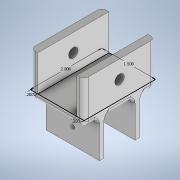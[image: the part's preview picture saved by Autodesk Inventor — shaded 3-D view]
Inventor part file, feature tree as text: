
AUTODESK INVENTOR PART (.ipt)
format: ipt  version: 2020 (Build 240168000, 168)  size: 201,728 bytes
history: native  units: in
note: dims shown in document units (in); Inventor stores cm internally (conversion verified against a paired STEP export)
features: sketch x4, extrude x3, hole x2, fillet x1
ambient origin geometry x8: Origin, YZ Plane, XZ Plane, XY Plane, X Axis, Y Axis, Z Axis, Center Point
bodies: Solid1 (feature_tree)
feature tree (10):
  sketch  "Sketch1"  dims[d0=1.5in d1=2.0in]
  extrude  "Extrusion1"  Depth=2.0in
  extrude  "Extrusion2"  Depth=0.2in
  hole  "Hole1"  [1 undecoded]
  extrude  "Extrusion3"  Depth=0.125in
  hole  "Hole2"  [1 undecoded]
  fillet  "Fillet1"  Radius=0.75in
  sketch  "Sketch2"  dims[d2=0.2in d3=0.2in]
  sketch  "Sketch3"  dims[d4=1.0in d5=0.0in d6=0.2in d7=0.0in]
  sketch  "Sketch4"  dims[d8=0.5in d9=0.266in d10=0.75in d11=0.438in d12=0.25in d13=0.5635in d14=1.0in d15=0.8108in d16=0.5in d17=1.0in d18=0.75in d19=0.125in d20=0.125in d21=1.0in d22=0.0in d23=0.45in d24=0.1125in d25=0.75in d26=0.438in d27=0.25in d28=0.5635in d29=1.0in d30=0.8108in d31=0.125in]
note: 2 required parameter values undecoded (feature->parameter linkage not recoverable at this tier; creation-order binding heuristic only, values carry confidence <= 0.55)
